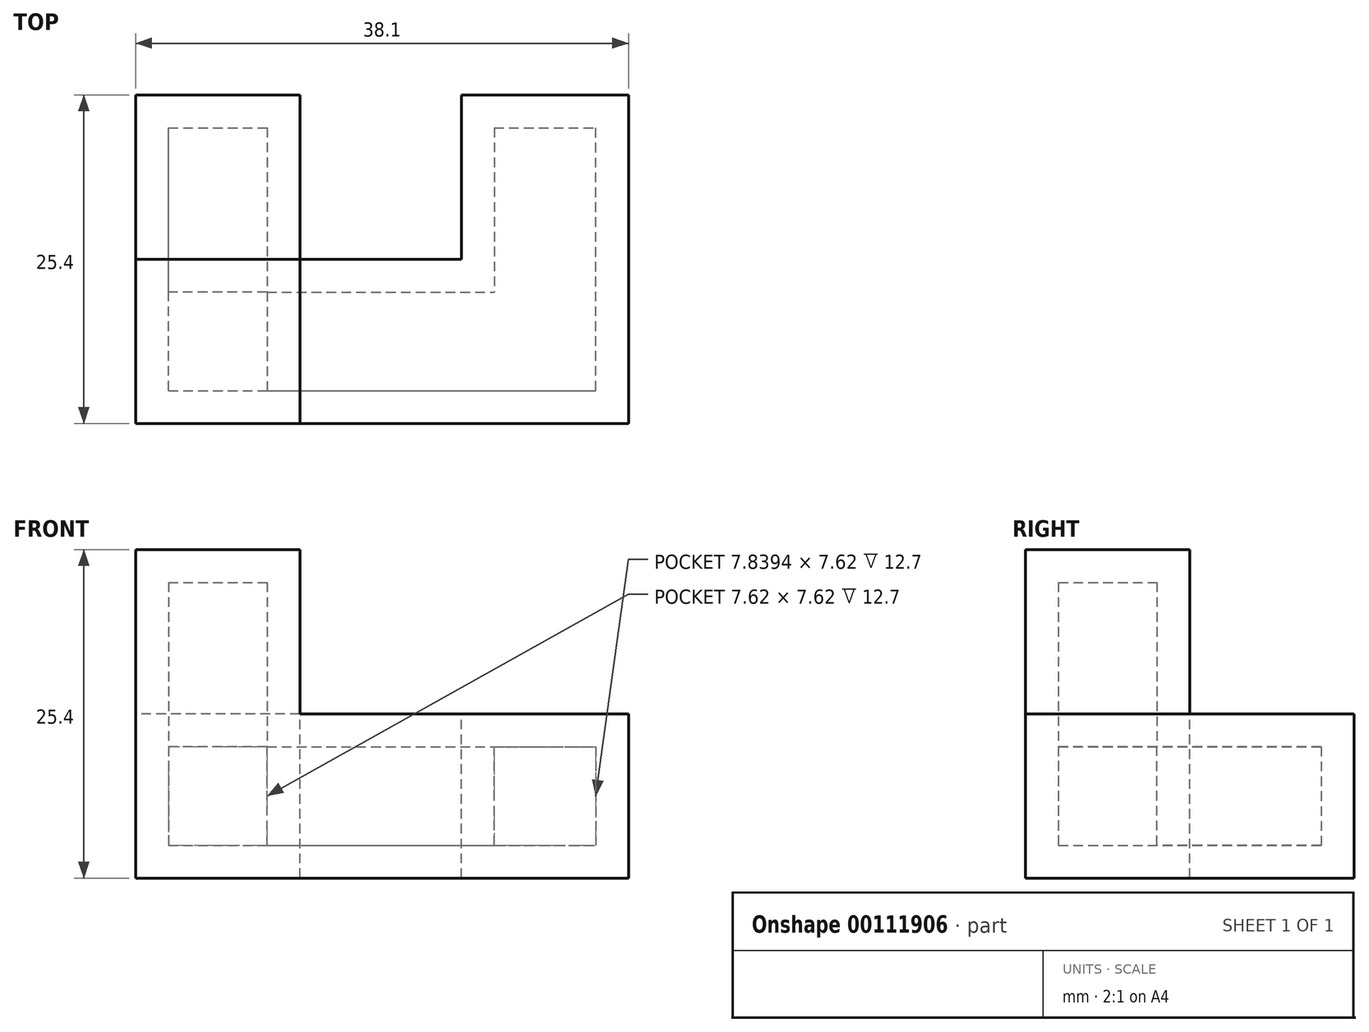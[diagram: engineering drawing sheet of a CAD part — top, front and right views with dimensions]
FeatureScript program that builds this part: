
annotation { "Feature Type Name" : "Feature", "Feature Type Description" : "" }
export const myFeature = defineFeature(function(context is Context, id is Id, definition is map)
    precondition{}
    {
        {
            var Q0;
            Q0=qCreatedBy(makeId("Front.planeOp"),FACE);
            var sketch = newSketch(context, id + "F0", { "sketchPlane" : qUnion([Q0])});
            skLineSegment(sketch, "E0.bottom", {"start": v(-5.87, 10.02) * mm, "end": v(6.83, 10.02) * mm});
            skLineSegment(sketch, "E0.top", {"start": v(-5.87, -2.68) * mm, "end": v(6.83, -2.68) * mm});
            skLineSegment(sketch, "E0.left", {"start": v(-5.87, 10.02) * mm, "end": v(-5.87, -2.68) * mm});
            skLineSegment(sketch, "E0.right", {"start": v(6.83, 10.02) * mm, "end": v(6.83, -2.68) * mm});
            skSolve(sketch);
        }
        {
            var Q0;
            Q0 = qSketchRegion(id + "F0", true);
            extrude(context, id + "F1", {"entities" : qUnion([Q0]), "depth" : 12.7 * mm});
        }
        {
            var Q0;
            Q0=makeQuery(id+"F1.opExtrude","SWEPT_FACE",FACE,{"disambiguationData":[OSD([sQuery(id+"F0.wireOp",EDGE,"E0.right")])]});
            extrude(context, id + "F2", {"entities" : qUnion([Q0]), "operationType" : NewBodyOperationType.ADD, "depth" : 25.4 * mm});
        }
        {
            var Q0;
            {var subQ0=sQuery(id+"F0.wireOp",EDGE,"E0.right");Q0=makeQuery(id+"F2.boolean.opBoolean","MERGE",FACE,{"derivedFrom":[makeQuery(id+"F1.opExtrude","CAP_FACE",FACE,{"disambiguationData":[OSD([sQuery(id+"F0.wireOp",EDGE,"E0.bottom"),sQuery(id+"F0.wireOp",EDGE,"E0.top"),sQuery(id+"F0.wireOp",EDGE,"E0.left"),subQ0])],"isStart":true}),makeQuery(id+"F2.opExtrude","SWEPT_FACE",FACE,{"disambiguationData":[OSD([subQ0]),TDD([makeQuery(id+"F1.opExtrude","CAP_EDGE",EDGE,{"disambiguationData":[OSD([subQ0])],"isStart":true})])]})]});}
            var sketch = newSketch(context, id + "F3", { "sketchPlane" : qUnion([Q0])});
            skLineSegment(sketch, "E1", {"start": v(-32.23, -2.68) * mm, "end": v(-19.3, -2.68) * mm});
            skLineSegment(sketch, "E2", {"start": v(-19.3, -2.68) * mm, "end": v(-19.3, 10.02) * mm});
            skLineSegment(sketch, "E3", {"start": v(5.87, -2.68) * mm, "end": v(-6.84, -2.68) * mm});
            skLineSegment(sketch, "E4", {"start": v(-6.84, -2.68) * mm, "end": v(-6.84, 10.02) * mm});
            skSolve(sketch);
        }
        {
            var Q0;
            Q0 = qSketchRegion(id + "F3", true);
            var Q1;
            Q1=makeQuery(id+"F3.imprint","IMPRINT",FACE,{"disambiguationData":[TD([[makeQuery(id+"F3.imprint","IMPRINT",EDGE,{"derivedFrom":sQuery(id+"F3.wireOp",EDGE,"E1")}),-1.0]])]});
            extrude(context, id + "F4", {"entities" : qUnion([Q0, Q1]), "operationType" : NewBodyOperationType.ADD, "depth" : 12.7 * mm});
        }
        {
            var Q0;
            {var subQ0=sQuery(id+"F0.wireOp",EDGE,"E0.right");Q0=makeQuery(id+"F2.boolean.opBoolean","MERGE",FACE,{"derivedFrom":[makeQuery(id+"F1.opExtrude","CAP_FACE",FACE,{"disambiguationData":[OSD([sQuery(id+"F0.wireOp",EDGE,"E0.bottom"),sQuery(id+"F0.wireOp",EDGE,"E0.top"),sQuery(id+"F0.wireOp",EDGE,"E0.left"),subQ0])],"isStart":true}),makeQuery(id+"F2.opExtrude","SWEPT_FACE",FACE,{"disambiguationData":[OSD([subQ0]),TDD([makeQuery(id+"F1.opExtrude","CAP_EDGE",EDGE,{"disambiguationData":[OSD([subQ0])],"isStart":true})])]})]});}
            var sketch = newSketch(context, id + "F5", { "sketchPlane" : qUnion([Q0])});
            skLineSegment(sketch, "E5", {"start": v(5.87, -2.68) * mm, "end": v(-6.83, -2.68) * mm});
            skLineSegment(sketch, "E6", {"start": v(-6.83, -2.68) * mm, "end": v(-6.83, 10.02) * mm});
            skSolve(sketch);
        }
        {
            var Q0;
            Q0 = qSketchRegion(id + "F5", true);
            var Q1;
            Q1=makeQuery(id+"F5.imprint","IMPRINT",FACE,{"disambiguationData":[TD([[makeQuery(id+"F5.imprint","IMPRINT",EDGE,{"derivedFrom":sQuery(id+"F5.wireOp",EDGE,"E5")}),-1.0]])]});
            extrude(context, id + "F6", {"entities" : qUnion([Q0, Q1]), "operationType" : NewBodyOperationType.ADD, "depth" : 12.7 * mm});
        }
        {
            var Q0;
            {var subQ0=sQuery(id+"F0.wireOp",EDGE,"E0.right");var subQ1=sQuery(id+"F0.wireOp",EDGE,"E0.bottom");Q0=makeQuery(id+"F6.boolean.opBoolean","MERGE",FACE,{"derivedFrom":[makeQuery(id+"F4.boolean.opBoolean","MERGE",FACE,{"derivedFrom":[makeQuery(id+"F2.boolean.opBoolean","MERGE",FACE,{"derivedFrom":[makeQuery(id+"F1.opExtrude","SWEPT_FACE",FACE,{"disambiguationData":[OSD([subQ1])]}),makeQuery(id+"F2.opExtrude","SWEPT_FACE",FACE,{"disambiguationData":[OSD([subQ1,subQ0])]})]}),makeQuery(id+"F4.opExtrude","SWEPT_FACE",FACE,{"disambiguationData":[OSD([subQ1,subQ0])]})]}),makeQuery(id+"F6.opExtrude","SWEPT_FACE",FACE,{"disambiguationData":[OSD([subQ1,subQ0])]})]});}
            var sketch = newSketch(context, id + "F7", { "sketchPlane" : qUnion([Q0])});
            skLineSegment(sketch, "E7", {"start": v(6.83, 0) * mm, "end": v(-5.87, 0) * mm});
            skLineSegment(sketch, "E8", {"start": v(6.83, 0) * mm, "end": v(6.83, -12.7) * mm});
            skSolve(sketch);
        }
        {
            var Q0;
            Q0 = qSketchRegion(id + "F7", true);
            var Q1;
            {var subQ0=sQuery(id+"F7.wireOp",EDGE,"E7");Q1=makeQuery(id+"F7.imprint","IMPRINT",FACE,{"disambiguationData":[TD([[makeQuery(id+"F7.imprint","IMPRINT",EDGE,{"derivedFrom":subQ0}),1.0]])]});}
            extrude(context, id + "F8", {"entities" : qUnion([Q0, Q1]), "operationType" : NewBodyOperationType.ADD, "depth" : 12.7 * mm});
        }
        {
            var Q0;
            {var subQ0=sQuery(id+"F0.wireOp",EDGE,"E0.right");Q0=makeQuery(id+"F4.boolean.opBoolean","MERGE",FACE,{"derivedFrom":[makeQuery(id+"F2.opExtrude","CAP_FACE",FACE,{"disambiguationData":[OSD([subQ0])],"isStart":false}),makeQuery(id+"F4.opExtrude","SWEPT_FACE",FACE,{"disambiguationData":[OSD([subQ0])]})]});}
            var Q1;
            Q1=makeQuery(id+"F1.opExtrude","SWEPT_BODY",BODY,{"disambiguationData":[OSD([sQuery(id+"F0.wireOp",EDGE,"E0.bottom"),sQuery(id+"F0.wireOp",EDGE,"E0.top"),sQuery(id+"F0.wireOp",EDGE,"E0.left"),sQuery(id+"F0.wireOp",EDGE,"E0.right")])]});
            shell(context, id + "F9", {"isHollow" : true, "entities" : qUnion([Q0]), "parts" : qUnion([Q1]), "thickness" : 2.54 * mm});
        }
    });
